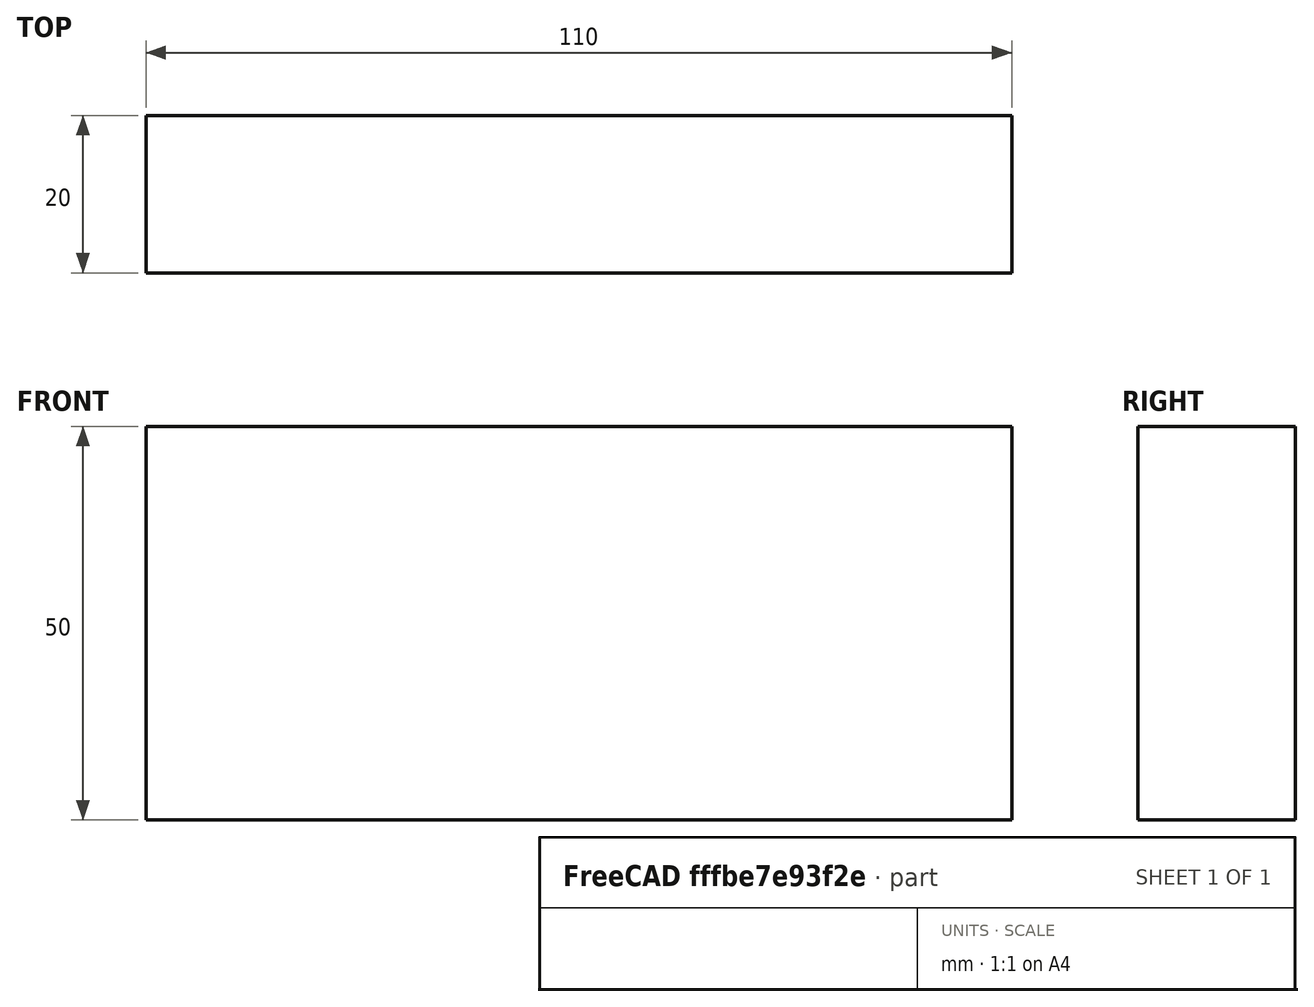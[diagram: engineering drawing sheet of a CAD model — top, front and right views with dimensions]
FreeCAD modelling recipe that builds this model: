
FCSTD DOCUMENT  (FreeCAD 0.15R4671 (Git))
Label: Flat Bar 110x20 EN10058 S235JR
License: All rights reserved
LicenseURL: http://en.wikipedia.org/wiki/All_rights_reserved
objects: Sketcher::SketchObject×1, Part::Extrusion×1
note: 2 computed .brp shape members not serialized (recipe doc carries the construction recipe); baked Part::Feature solids carry a one-line shape summary decoded from their .brp

FEATURE [Sketcher::SketchObject] Sketch
  sketch-geometry (4):
    g0: LineSegment StartX=-55 StartY=-10 StartZ=0 EndX=55 EndY=-10 EndZ=0
    g1: LineSegment StartX=55 StartY=-10 StartZ=0 EndX=55 EndY=10 EndZ=0
    g2: LineSegment StartX=55 StartY=10 StartZ=0 EndX=-55 EndY=10 EndZ=0
    g3: LineSegment StartX=-55 StartY=10 StartZ=0 EndX=-55 EndY=-10 EndZ=0
  constraints (12):
    c: Coincident(g0,g1)
    c: Coincident(g1,g2)
    c: Coincident(g2,g3)
    c: Coincident(g3,g0)
    c: Horizontal(g0)
    c: Horizontal(g2)
    c: Vertical(g1)
    c: Vertical(g3)
    c: Symmetric(g1,g2,g-2)
    c: Symmetric(g0,g1,g-1)
    c: DistanceY(g1) = 20
    c: DistanceX(g0) = 110
FEATURE [Part::Extrusion] Extrude  label="Flat Bar 110x20 EN10058 S235JR"
  Base = -> Sketch
  Dir = (0,0,50)
  Solid = true
